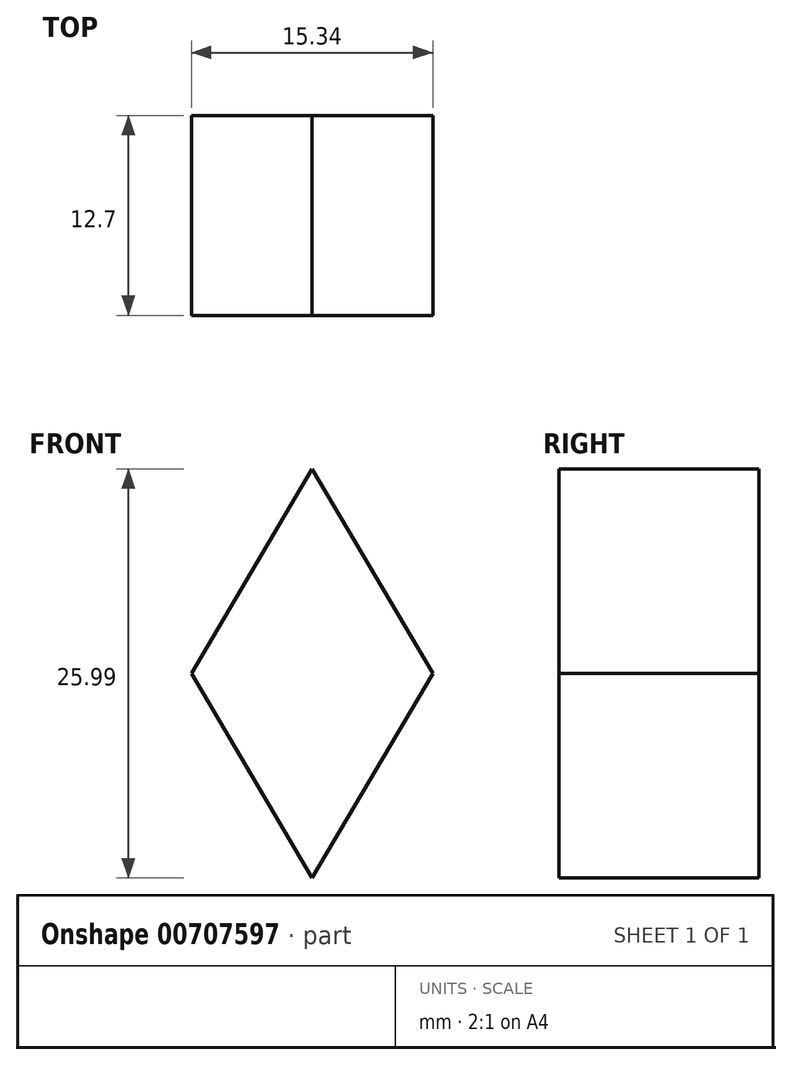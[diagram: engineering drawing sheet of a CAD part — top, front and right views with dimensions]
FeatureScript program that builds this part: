
annotation { "Feature Type Name" : "Feature", "Feature Type Description" : "" }
export const myFeature = defineFeature(function(context is Context, id is Id, definition is map)
    precondition{}
    {
        {
            var Q0;
            Q0=qCreatedBy(makeId("Front.planeOp"),FACE);
            var sketch = newSketch(context, id + "F0", { "sketchPlane" : qUnion([Q0])});
            skLineSegment(sketch, "E0", {"start": v(11.7, 8.56) * mm, "end": v(10.7, -7.18) * mm});
            skLineSegment(sketch, "E1", {"start": v(10.7, -7.18) * mm, "end": v(-10.6, 19) * mm});
            skLineSegment(sketch, "E2", {"start": v(-10.6, 19) * mm, "end": v(-7.8, 82.36) * mm});
            skFitSpline(sketch, "E3", {"points": [v(-7.8, 82.36) * mm, v(-7.24, 98.94) * mm, v(-6.59, 117.12) * mm, v(-5.83, 142.02) * mm, v(-5.45, 168.32) * mm, v(-5.52, 230.34) * mm, v(-6.26, 285.7) * mm, v(-7.2, 315.28) * mm, v(-8.95, 361.43) * mm, v(-10.4, 387.63) * mm, v(-13, 416.84) * mm, v(-15.01, 437.7) * mm, v(-21.29, 480.96) * mm, v(-27.2, 508.68) * mm, v(-28.7, 514.88) * mm], "startDerivative": vector(10.22, 308.11) * mm, "endDerivative": vector(-37.95, 155.7) * mm});
            skLineSegment(sketch, "E4", {"start": v(-28.7, 514.88) * mm, "end": v(-18.5, 504.49) * mm});
            skFitSpline(sketch, "E5", {"points": [v(-18.5, 504.49) * mm, v(-14.2, 494.72) * mm, v(-10.4, 483.17) * mm, v(-6.54, 469.9) * mm, v(-3.1, 457.05) * mm, v(-0.51, 445.6) * mm, v(1.47, 435.93) * mm, v(2.96, 426.2) * mm, v(4.35, 415.6) * mm, v(5.85, 403.15) * mm, v(7.18, 390.92) * mm, v(9.67, 369.53) * mm, v(11.56, 352.56) * mm, v(15.2, 318.42) * mm, v(18.03, 290.8) * mm, v(19.92, 265.34) * mm, v(21.72, 242.6) * mm, v(22.69, 220.79) * mm, v(23.65, 203.25) * mm, v(24.47, 178.85) * mm, v(25.08, 148.77) * mm, v(25.19, 106.94) * mm, v(24.82, 74.57) * mm, v(24.5, 42) * mm], "startDerivative": vector(138.63, -295.52) * mm, "endDerivative": vector(-5.12, -584.15) * mm});
            skFitSpline(sketch, "E6", {"points": [v(24.5, 42) * mm, v(16.7, 39) * mm, v(12.5, 33.24) * mm, v(9.61, 24.95) * mm, v(8.9, 16.91) * mm, v(10.33, 12.23) * mm, v(11.7, 8.56) * mm], "startDerivative": vector(-46.28, -12) * mm, "endDerivative": vector(10.21, -28.51) * mm});
            skFitSpline(sketch, "E7", {"points": [v(-10.6, 84.98) * mm, v(-8.5, 83) * mm, v(-6.65, 78.8) * mm, v(-5.89, 72.07) * mm, v(-5.76, 61.33) * mm, v(-5.64, 47.1) * mm, v(-5.9, 35.6) * mm, v(-6.47, 31.43) * mm, v(-6.34, 26.97) * mm, v(-4.57, 21.8) * mm, v(-2.21, 17.83) * mm, v(0, 15.05) * mm, v(2.28, 13.08) * mm, v(5.76, 11.32) * mm, v(8.69, 10.16) * mm, v(11.04, 8.9) * mm, v(12.38, 7.6) * mm, v(13.09, 5.99) * mm, v(12.89, 2.76) * mm, v(12.15, -3.9) * mm, v(11.7, -8.74) * mm, v(11.08, -13.22) * mm], "startDerivative": vector(59.9, -45.86) * mm, "endDerivative": vector(-14.62, -97.53) * mm});
            skLineSegment(sketch, "E8", {"start": v(11.08, -13.22) * mm, "end": v(11.08, -15.97) * mm});
            skLineSegment(sketch, "E9", {"start": v(11.08, -15.97) * mm, "end": v(-11.03, -15.97) * mm});
            skLineSegment(sketch, "E10", {"start": v(-11.03, -15.97) * mm, "end": v(-11.2, -13.29) * mm});
            skFitSpline(sketch, "E11", {"points": [v(-11.2, -13.29) * mm, v(-11.2, -11.84) * mm, v(-11.2, -5.52) * mm, v(-11.51, 1.49) * mm, v(-12.16, 4.66) * mm, v(-13.4, 9.05) * mm, v(-15.15, 13.55) * mm, v(-16.64, 17.33) * mm, v(-19.12, 23.61) * mm, v(-19.55, 26.56) * mm, v(-18.64, 31.28) * mm, v(-16.79, 35.33) * mm, v(-14.77, 40.57) * mm, v(-13.5, 46.17) * mm, v(-12.6, 53.4) * mm, v(-12.2, 59.96) * mm, v(-12.37, 65.97) * mm, v(-12.16, 73.91) * mm, v(-11.5, 81.04) * mm, v(-11.2, 84.64) * mm, v(-10.6, 84.98) * mm], "startDerivative": vector(-0.12, 43.3) * mm, "endDerivative": vector(35.61, 8.6) * mm});
            skFitSpline(sketch, "E12", {"points": [v(11.08, -13.22) * mm, v(15.57, -17.52) * mm, v(22.06, -24.41) * mm, v(29.6, -33.47) * mm, v(35.84, -41.56) * mm, v(40.17, -47.64) * mm, v(44.57, -55.74) * mm, v(47.94, -62.06) * mm, v(51.06, -67.51) * mm, v(52.42, -69.67) * mm, v(49.81, -81.38) * mm, v(45.5, -94.07) * mm, v(41.24, -106.63) * mm, v(36.2, -120.43) * mm, v(32.84, -130.03) * mm, v(29.35, -138.2) * mm, v(27.78, -142.23) * mm, v(23.27, -152.08) * mm, v(21.3, -154.75) * mm, v(16.02, -157.43) * mm, v(8.58, -160.03) * mm, v(4.77, -160.41) * mm, v(4.83, -154.75) * mm, v(8.26, -152.78) * mm, v(13.03, -150.3) * mm, v(16.97, -147.44) * mm, v(20.66, -141.85) * mm, v(25.37, -129.07) * mm, v(31.66, -108.36) * mm, v(36.51, -89.69) * mm, v(39.56, -77.02) * mm, v(39.75, -72.83) * mm, v(38.74, -67.42) * mm, v(35.21, -61.22) * mm, v(28.26, -50.55) * mm, v(23.02, -43.89) * mm, v(18.43, -38.21) * mm, v(13.22, -32.69) * mm, v(7.93, -27.32) * mm, v(6.6, -20.94) * mm, v(11.08, -13.22) * mm]});
            skLineSegment(sketch, "E13.bottom", {"start": v(-12.44, -13.29) * mm, "end": v(11.54, -13.29) * mm});
            skLineSegment(sketch, "E13.top", {"start": v(-12.44, -29.01) * mm, "end": v(11.54, -29.01) * mm});
            skLineSegment(sketch, "E13.left", {"start": v(-12.44, -13.29) * mm, "end": v(-12.44, -29.01) * mm});
            skLineSegment(sketch, "E13.right", {"start": v(11.54, -13.29) * mm, "end": v(11.54, -29.01) * mm});
            skLineSegment(sketch, "E14", {"start": v(0, -32.56) * mm, "end": v(0, -38.28) * mm});
            skFitSpline(sketch, "E15", {"points": [v(-10.75, -28.03) * mm, v(-9.93, -35.6) * mm, v(-9.25, -45.2) * mm, v(-8.25, -64.06) * mm, v(-7.6, -83.45) * mm, v(-7.55, -95.02) * mm, v(-7.45, -109.5) * mm, v(-7.73, -122.65) * mm, v(-8.29, -138.57) * mm, v(-9.14, -152.56) * mm, v(-9.03, -155.04) * mm], "startDerivative": vector(11.05, -94.6) * mm, "endDerivative": vector(4.37, -43.01) * mm});
            skLineSegment(sketch, "E16", {"start": v(-9.9, -153.6) * mm, "end": v(9.57, -153.6) * mm});
            skFitSpline(sketch, "E17.MirrorCS", {"points": [v(10.75, -28.03) * mm, v(9.93, -35.6) * mm, v(9.25, -45.2) * mm, v(8.25, -64.06) * mm, v(7.6, -83.45) * mm, v(7.55, -95.02) * mm, v(7.45, -109.5) * mm, v(7.73, -122.65) * mm, v(8.29, -138.57) * mm, v(9.14, -152.56) * mm, v(9.03, -155.04) * mm], "startDerivative": vector(-11.05, -94.6) * mm, "endDerivative": vector(-4.37, -43.01) * mm});
            skSolve(sketch);
        }
        {
            var Q0;
            {var subQ4=sQuery(id+"F0.wireOp",EDGE,"E1");Q0=makeQuery(id+"F0.imprint","IMPRINT",FACE,{"disambiguationData":[TD([[makeQuery(id+"F0.imprint","IMPRINT",EDGE,{"derivedFrom":subQ4}),1.0]])]});}
            var Q1;
            {var subQ0=sQuery(id+"F0.wireOp",EDGE,"E1");Q1=makeQuery(id+"F0.imprint","IMPRINT",FACE,{"disambiguationData":[TD([[makeQuery(id+"F0.imprint","IMPRINT",EDGE,{"derivedFrom":subQ0}),-1.0]])]});}
            var Q2;
            {var subQ0=sQuery(id+"F0.wireOp",EDGE,"E9");var subQ1=sQuery(id+"F0.wireOp",EDGE,"E8");var subQ2=makeQuery(id+"F0.imprint","INTERSECT",VERTEX,{"derivedFrom":[subQ1,subQ0]});Q2=makeQuery(id+"F0.imprint","IMPRINT",FACE,{"disambiguationData":[TD([[makeQuery(id+"F0.imprint","IMPRINT",EDGE,{"disambiguationData":[TD([[subQ2,1.0]])],"derivedFrom":subQ1}),-1.0]])]});}
            var Q3;
            {var subQ0=sQuery(id+"F0.wireOp",EDGE,"E10");Q3=makeQuery(id+"F0.imprint","IMPRINT",FACE,{"disambiguationData":[TD([[makeQuery(id+"F0.imprint","IMPRINT",EDGE,{"derivedFrom":subQ0}),-1.0]])]});}
            var Q4;
            {var subQ1=sQuery(id+"F0.wireOp",EDGE,"E8");var subQ3=sQuery(id+"F0.wireOp",EDGE,"E13.bottom");var subQ4=makeQuery(id+"F0.imprint","INTERSECT",VERTEX,{"derivedFrom":[subQ1,subQ3]});Q4=makeQuery(id+"F0.imprint","IMPRINT",FACE,{"disambiguationData":[TD([[makeQuery(id+"F0.imprint","IMPRINT",EDGE,{"disambiguationData":[TD([[subQ4,1.0]])],"derivedFrom":subQ3}),1.0]])]});}
            extrude(context, id + "F1", {"entities" : qUnion([Q0, Q1, Q2, Q3, Q4]), "depth" : 5.08 * mm, "offsetDistance" : 25.4 * mm});
        }
        {
            var Q0;
            Q0=makeQuery(id+"F1.opExtrude","CAP_FACE",FACE,{"disambiguationData":[OSD([sQuery(id+"F0.wireOp",EDGE,"E7"),sQuery(id+"F0.wireOp",EDGE,"E11"),sQuery(id+"F0.wireOp",EDGE,"E12"),sQuery(id+"F0.wireOp",EDGE,"E13.bottom")])],"isStart":true});
            extrude(context, id + "F2", {"entities" : qUnion([Q0]), "operationType" : NewBodyOperationType.ADD, "depth" : 5.08 * mm, "offsetDistance" : 25.4 * mm});
        }
        {
            var Q0;
            Q0=makeQuery(id+"F1.opExtrude","CAP_FACE",FACE,{"disambiguationData":[OSD([sQuery(id+"F0.wireOp",EDGE,"E7"),sQuery(id+"F0.wireOp",EDGE,"E8"),sQuery(id+"F0.wireOp",EDGE,"E9"),sQuery(id+"F0.wireOp",EDGE,"E10"),sQuery(id+"F0.wireOp",EDGE,"E11")])],"isStart":false});
            var sketch = newSketch(context, id + "F3", { "sketchPlane" : qUnion([Q0])});
            skLineSegment(sketch, "E18", {"start": v(0, 13) * mm, "end": v(7.67, 0) * mm});
            skLineSegment(sketch, "E19", {"start": v(7.67, 0) * mm, "end": v(0, -13) * mm});
            skLineSegment(sketch, "E20", {"start": v(0, -13) * mm, "end": v(0, -9.64) * mm});
            skLineSegment(sketch, "E21.MirrorCS", {"start": v(-7.67, 0) * mm, "end": v(0, -13) * mm});
            skLineSegment(sketch, "E22.MirrorCS", {"start": v(0, 13) * mm, "end": v(-7.67, 0) * mm});
            skLineSegment(sketch, "E23.bottom", {"start": v(-55.21, 97.24) * mm, "end": v(69.67, 97.24) * mm});
            skLineSegment(sketch, "E23.top", {"start": v(-55.21, -36.84) * mm, "end": v(69.67, -36.84) * mm});
            skLineSegment(sketch, "E23.left", {"start": v(-55.21, 97.24) * mm, "end": v(-55.21, -36.84) * mm});
            skLineSegment(sketch, "E23.right", {"start": v(69.67, 97.24) * mm, "end": v(69.67, -36.84) * mm});
            skSolve(sketch);
        }
        {
            var Q0;
            Q0=makeQuery(id+"F3.imprint","IMPRINT",FACE,{"disambiguationData":[TD([[makeQuery(id+"F3.imprint","IMPRINT",EDGE,{"derivedFrom":sQuery(id+"F3.wireOp",EDGE,"E23.bottom")}),-1.0]])]});
            var Q1;
            Q1=makeQuery(id+"F3.imprint","IMPRINT",FACE,{"disambiguationData":[TD([[makeQuery(id+"F3.imprint","IMPRINT",EDGE,{"derivedFrom":sQuery(id+"F3.wireOp",EDGE,"E18")}),1.0]])]});
            extrude(context, id + "F4", {"entities" : qUnion([Q0, Q1]), "operationType" : NewBodyOperationType.REMOVE, "oppositeDirection" : true, "depth" : 25.4 * mm, "offsetDistance" : 25.4 * mm});
        }
        {
            var Q0;
            Q0=makeQuery(id+"F1.opExtrude","CAP_FACE",FACE,{"disambiguationData":[OSD([sQuery(id+"F0.wireOp",EDGE,"E7"),sQuery(id+"F0.wireOp",EDGE,"E8"),sQuery(id+"F0.wireOp",EDGE,"E9"),sQuery(id+"F0.wireOp",EDGE,"E10"),sQuery(id+"F0.wireOp",EDGE,"E11")])],"isStart":false});
            extrude(context, id + "F5", {"entities" : qUnion([Q0]), "operationType" : NewBodyOperationType.ADD, "depth" : 1.27 * mm, "offsetDistance" : 25.4 * mm});
        }
        {
            var Q0;
            Q0=makeQuery(id+"F2.opExtrude","CAP_FACE",FACE,{"disambiguationData":[OSD([sQuery(id+"F0.wireOp",EDGE,"E7"),sQuery(id+"F0.wireOp",EDGE,"E8"),sQuery(id+"F0.wireOp",EDGE,"E9"),sQuery(id+"F0.wireOp",EDGE,"E10"),sQuery(id+"F0.wireOp",EDGE,"E11")])],"isStart":false});
            extrude(context, id + "F6", {"entities" : qUnion([Q0]), "operationType" : NewBodyOperationType.ADD, "depth" : 1.27 * mm, "offsetDistance" : 25.4 * mm});
        }
    });
